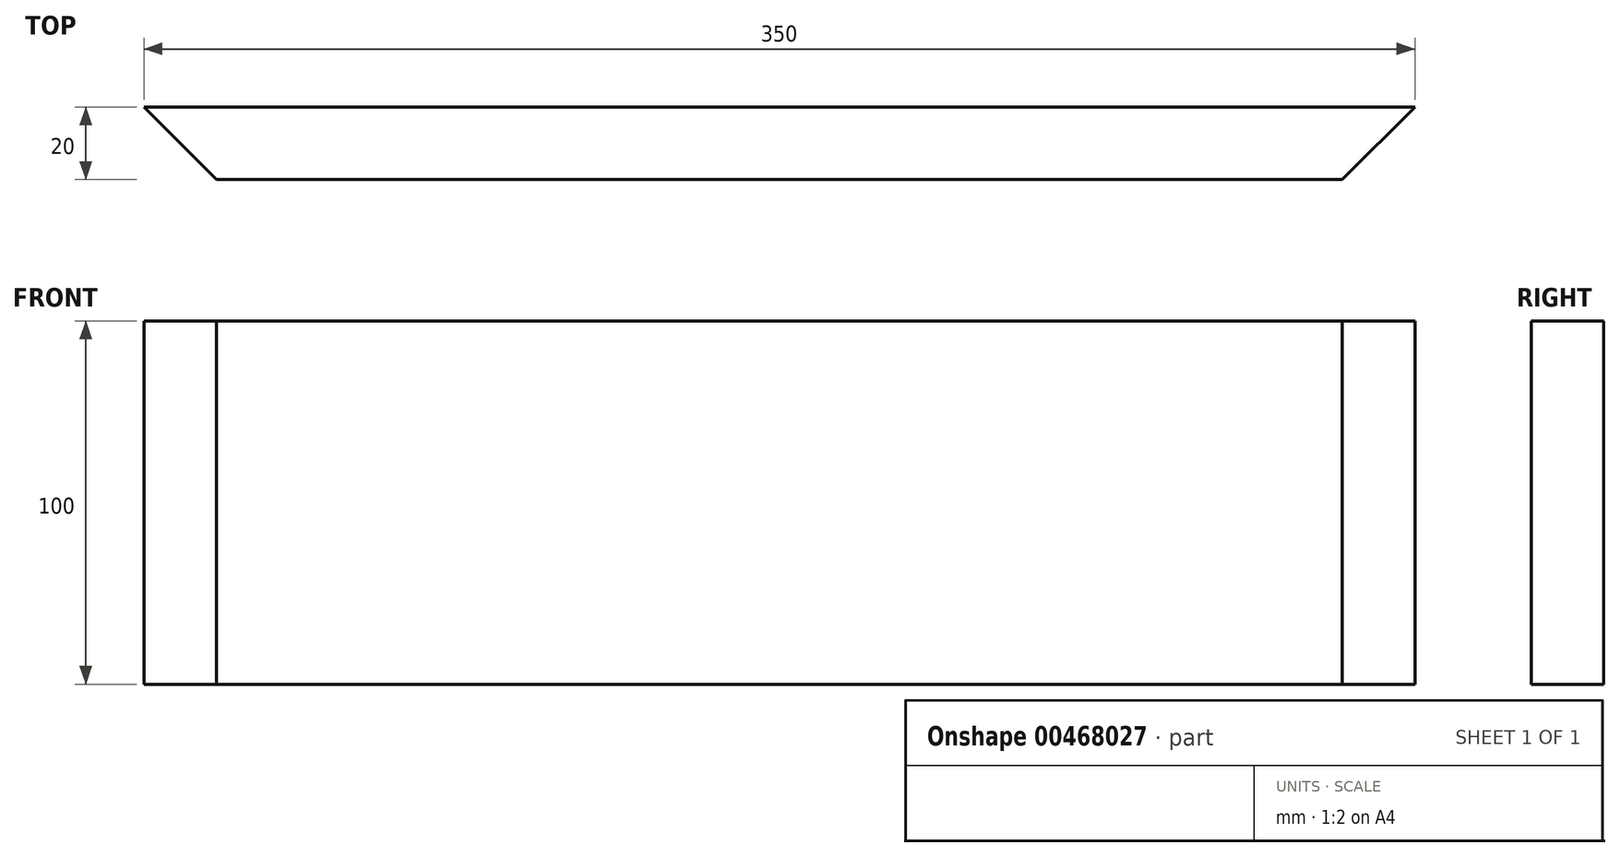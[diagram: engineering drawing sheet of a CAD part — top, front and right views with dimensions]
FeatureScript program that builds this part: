
annotation { "Feature Type Name" : "Feature", "Feature Type Description" : "" }
export const myFeature = defineFeature(function(context is Context, id is Id, definition is map)
    precondition{}
    {
        {
            var Q0;
            Q0=qCreatedBy(makeId("Front.planeOp"),FACE);
            var sketch = newSketch(context, id + "F0", { "sketchPlane" : qUnion([Q0])});
            skLineSegment(sketch, "E0.bottom", {"start": v(0, 0) * mm, "end": v(350, 0) * mm});
            skLineSegment(sketch, "E0.top", {"start": v(0, 100) * mm, "end": v(350, 100) * mm});
            skLineSegment(sketch, "E0.left", {"start": v(0, 0) * mm, "end": v(0, 100) * mm});
            skLineSegment(sketch, "E0.right", {"start": v(350, 0) * mm, "end": v(350, 100) * mm});
            skSolve(sketch);
        }
        {
            var Q0;
            Q0 = qSketchRegion(id + "F0", true);
            var Q1;
            Q1=makeQuery(id+"F0.imprint","IMPRINT",FACE,{"disambiguationData":[TD([[makeQuery(id+"F0.imprint","IMPRINT",EDGE,{"derivedFrom":sQuery(id+"F0.wireOp",EDGE,"E0.bottom")}),1.0]])]});
            extrude(context, id + "F1", {"entities" : qUnion([Q0, Q1]), "endBound" : BoundingType.SYMMETRIC, "depth" : 20 * mm});
        }
        {
            var Q0;
            Q0=makeQuery(id+"F1.opExtrude","CAP_EDGE",EDGE,{"disambiguationData":[OSD([sQuery(id+"F0.wireOp",EDGE,"E0.left")])],"isStart":false});
            chamfer(context, id + "F2", {"entities" : qUnion([Q0]), "chamferType" : ChamferType.OFFSET_ANGLE, "width" : 20 * mm, "oppositeDirection" : true, "angle" : 45 * degree, "tangentPropagation" : true});
        }
        {
            var Q0;
            Q0=makeQuery(id+"F1.opExtrude","CAP_EDGE",EDGE,{"disambiguationData":[OSD([sQuery(id+"F0.wireOp",EDGE,"E0.right")])],"isStart":false});
            chamfer(context, id + "F3", {"entities" : qUnion([Q0]), "chamferType" : ChamferType.OFFSET_ANGLE, "width" : 20 * mm, "oppositeDirection" : false, "angle" : 45 * degree, "tangentPropagation" : true});
        }
    });
